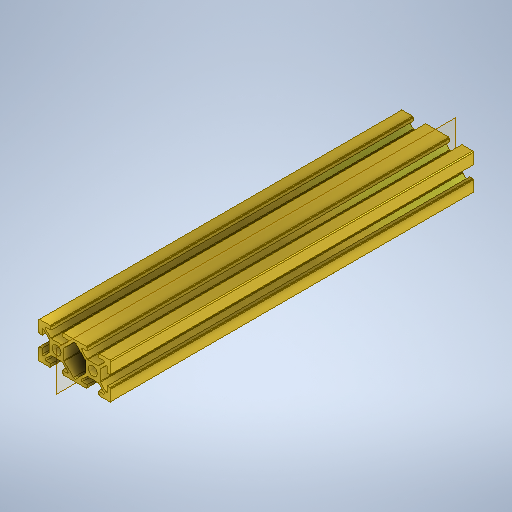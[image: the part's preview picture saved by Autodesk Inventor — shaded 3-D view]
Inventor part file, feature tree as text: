
AUTODESK INVENTOR PART (.ipt)
format: ipt  version: 2025.2 (Build 292293000, 293)  size: 443,392 bytes
history: native  units: mm
features: other x2, mirror x2, fillet x2, extrude x1, sketch x1
ambient origin geometry x8: Origin, YZ Plane, XZ Plane, XY Plane, X Axis, Y Axis, Z Axis, Center Point
bodies: Body1 (feature_tree)
feature tree (8):
  other  "Sólido1"
  extrude  "Extrusão1"  Depth=6.2mm
  mirror  "Espelhar3"
  mirror  "Espelhar4"
  fillet  "Arredondamento1"  Radius=5.0mm
  fillet  "Arredondamento2"  Radius=10.0mm
  other  "Plano de trabalho1"
  sketch  "Esboço1"  dims[d0=40.0mm d1=6.2mm d3=5.0mm d6=10.0mm d7=6.0mm d8=20.0mm d11=2.0mm d12=200.0mm d13=0.0mm d15=0.5mm d18=6.0mm d19=0.5mm d21=4.0mm d22=1.0mm d23=1.0mm]
